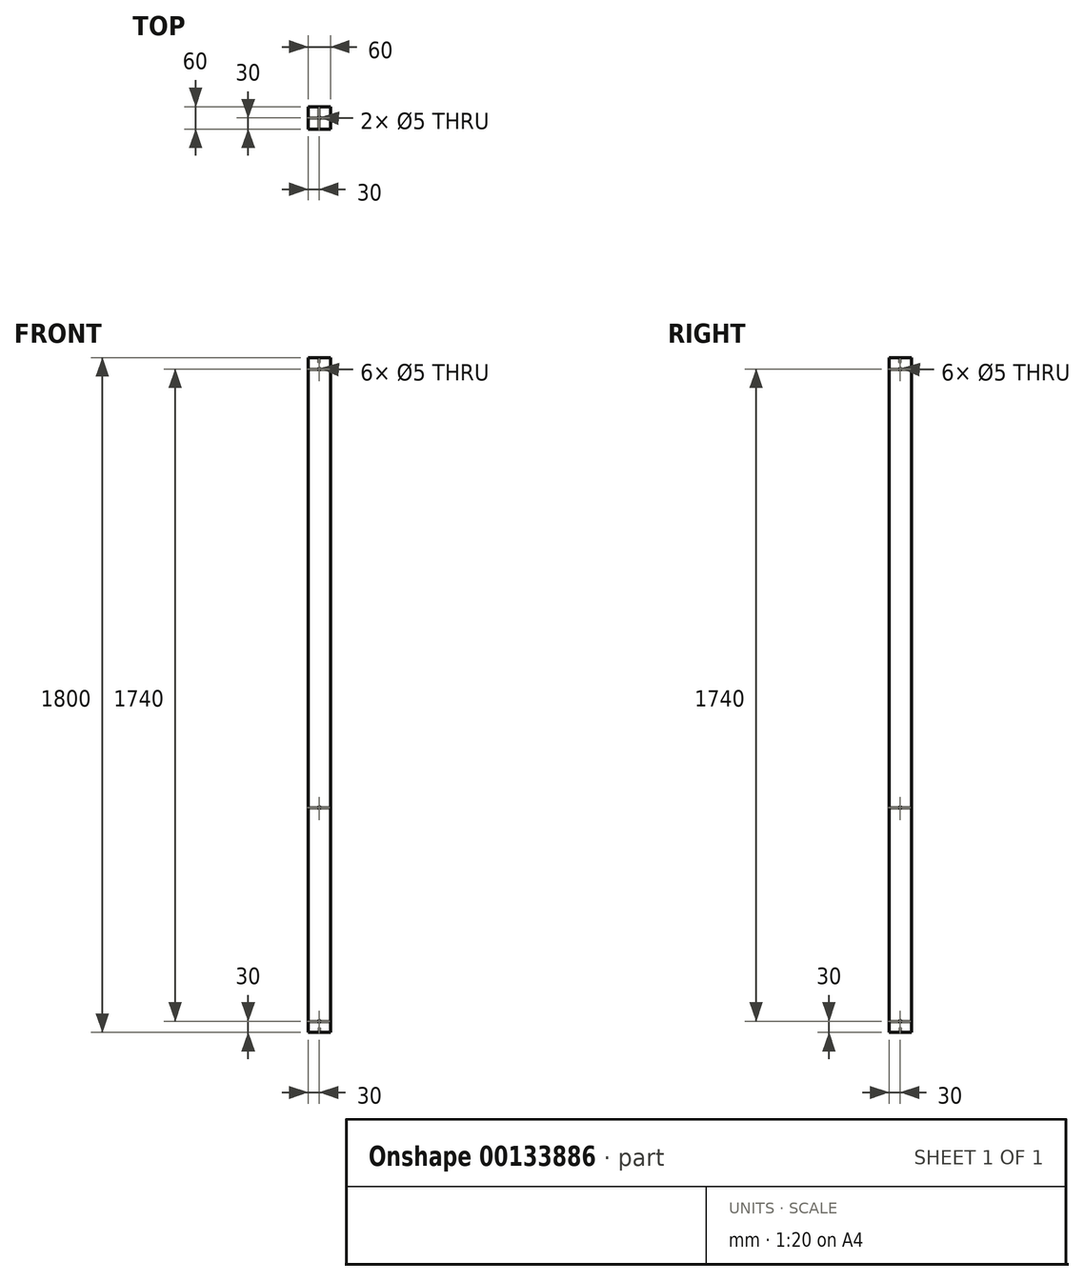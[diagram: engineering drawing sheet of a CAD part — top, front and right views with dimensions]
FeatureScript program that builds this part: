
annotation { "Feature Type Name" : "Feature", "Feature Type Description" : "" }
export const myFeature = defineFeature(function(context is Context, id is Id, definition is map)
    precondition{}
    {
        {
            assignVariable(context, id + "F0", {"name" : "Laenge", "anyValue" : 1800 * mm});
        }
        {
            var Q0;
            Q0=qCreatedBy(makeId("Top.planeOp"),FACE);
            var sketch = newSketch(context, id + "F1", { "sketchPlane" : qUnion([Q0])});
            skLineSegment(sketch, "E0.bottom", {"start": v(-30, 30) * mm, "end": v(30, 30) * mm});
            skLineSegment(sketch, "E0.top", {"start": v(-30, -30) * mm, "end": v(30, -30) * mm});
            skLineSegment(sketch, "E0.left", {"start": v(-30, 30) * mm, "end": v(-30, -30) * mm});
            skLineSegment(sketch, "E0.right", {"start": v(30, 30) * mm, "end": v(30, -30) * mm});
            skPoint(sketch, "E1", {"position": v(0, 30) * mm});
            skPoint(sketch, "E2", {"position": v(30, 0) * mm});
            skLineSegment(sketch, "E3", {"start": v(0, 30) * mm, "end": v(0, 0) * mm, "construction": true});
            skLineSegment(sketch, "E4", {"start": v(0, 0) * mm, "end": v(30, 0) * mm, "construction": true});
            skSolve(sketch);
        }
        {
            var Q0;
            Q0=qSketchRegion(id+"F1",true);
            extrude(context, id + "F2", {"entities" : qUnion([Q0]), "depth" : getVariable(context, 'Laenge')});
        }
        {
            var Q0;
            Q0=makeQuery(id+"F2.opExtrude","CAP_FACE",FACE,{"disambiguationData":[OSD([sQuery(id+"F1.wireOp",EDGE,"E0.bottom"),sQuery(id+"F1.wireOp",EDGE,"E0.top"),sQuery(id+"F1.wireOp",EDGE,"E0.left"),sQuery(id+"F1.wireOp",EDGE,"E0.right")])],"isStart":false});
            var sketch = newSketch(context, id + "F3", { "sketchPlane" : qUnion([Q0])});
            skPoint(sketch, "E5", {"position": v(0, 0) * mm});
            skSolve(sketch);
        }
        {
            var Q0;
            Q0=makeQuery(id+"F2.opExtrude","CAP_FACE",FACE,{"disambiguationData":[OSD([sQuery(id+"F1.wireOp",EDGE,"E0.bottom"),sQuery(id+"F1.wireOp",EDGE,"E0.top"),sQuery(id+"F1.wireOp",EDGE,"E0.left"),sQuery(id+"F1.wireOp",EDGE,"E0.right")])],"isStart":true});
            var sketch = newSketch(context, id + "F4", { "sketchPlane" : qUnion([Q0])});
            skPoint(sketch, "E6", {"position": v(0, 0) * mm});
            skSolve(sketch);
        }
        {
            var Q0;
            Q0=makeQuery(id+"F2.opExtrude","SWEPT_FACE",FACE,{"disambiguationData":[OSD([sQuery(id+"F1.wireOp",EDGE,"E0.right")])]});
            var sketch = newSketch(context, id + "F5", { "sketchPlane" : qUnion([Q0])});
            skPoint(sketch, "E7", {"position": v(0, 1770) * mm});
            skLineSegment(sketch, "E8", {"start": v(30, 900) * mm, "end": v(-30, 900) * mm, "construction": true});
            skPoint(sketch, "E9.MirrorP", {"position": v(0, 30) * mm});
            skPoint(sketch, "E10", {"position": v(0, 600) * mm});
            skSolve(sketch);
        }
        {
            var Q0;
            Q0=makeQuery(id+"F2.opExtrude","SWEPT_FACE",FACE,{"disambiguationData":[OSD([sQuery(id+"F1.wireOp",EDGE,"E0.bottom")])]});
            var sketch = newSketch(context, id + "F6", { "sketchPlane" : qUnion([Q0])});
            skPoint(sketch, "E11", {"position": v(0, 1770) * mm});
            skPoint(sketch, "E11.positionSnap0", {"position": v(0, 1800) * mm});
            skLineSegment(sketch, "E12", {"start": v(30, 900) * mm, "end": v(-30, 900) * mm, "construction": true});
            skPoint(sketch, "E13.MirrorP", {"position": v(0, 30) * mm});
            skPoint(sketch, "E14", {"position": v(0, 600) * mm});
            skSolve(sketch);
        }
        {
            var Q0;
            Q0=sQuery(id+"F3.wireOp",VERTEX,"E5");
            var Q1;
            Q1=sQuery(id+"F4.wireOp",VERTEX,"E6");
            var Q2;
            Q2=makeQuery(id+"F2.opExtrude","SWEPT_BODY",BODY,{"disambiguationData":[OSD([sQuery(id+"F1.wireOp",EDGE,"E0.bottom"),sQuery(id+"F1.wireOp",EDGE,"E0.top"),sQuery(id+"F1.wireOp",EDGE,"E0.left"),sQuery(id+"F1.wireOp",EDGE,"E0.right")])]});
            hole(context, id + "F7", {"style" : HoleStyle.SIMPLE, "endStyle" : HoleEndStyle.BLIND, "holeDiameter" : 5 * mm, "holeDepth" : 12 * mm, "startFromSketch" : true, "locations" : qUnion([Q0, Q1]), "scope" : qUnion([Q2])});
        }
        {
            var Q0;
            Q0=sQuery(id+"F6.wireOp",VERTEX,"E11");
            var Q1;
            Q1=sQuery(id+"F5.wireOp",VERTEX,"E7");
            var Q2;
            Q2=sQuery(id+"F5.wireOp",VERTEX,"E9.MirrorP");
            var Q3;
            Q3=sQuery(id+"F6.wireOp",VERTEX,"E13.MirrorP");
            var Q4;
            Q4=sQuery(id+"F6.wireOp",VERTEX,"E14");
            var Q5;
            Q5=sQuery(id+"F5.wireOp",VERTEX,"E10");
            var Q6;
            Q6=makeQuery(id+"F2.opExtrude","SWEPT_BODY",BODY,{"disambiguationData":[OSD([sQuery(id+"F1.wireOp",EDGE,"E0.bottom"),sQuery(id+"F1.wireOp",EDGE,"E0.top"),sQuery(id+"F1.wireOp",EDGE,"E0.left"),sQuery(id+"F1.wireOp",EDGE,"E0.right")])]});
            hole(context, id + "F8", {"style" : HoleStyle.SIMPLE, "endStyle" : HoleEndStyle.THROUGH, "holeDiameter" : 5 * mm, "startFromSketch" : true, "locations" : qUnion([Q0, Q1, Q2, Q3, Q4, Q5]), "scope" : qUnion([Q6]), "isTappedThrough" : true});
        }
    });
